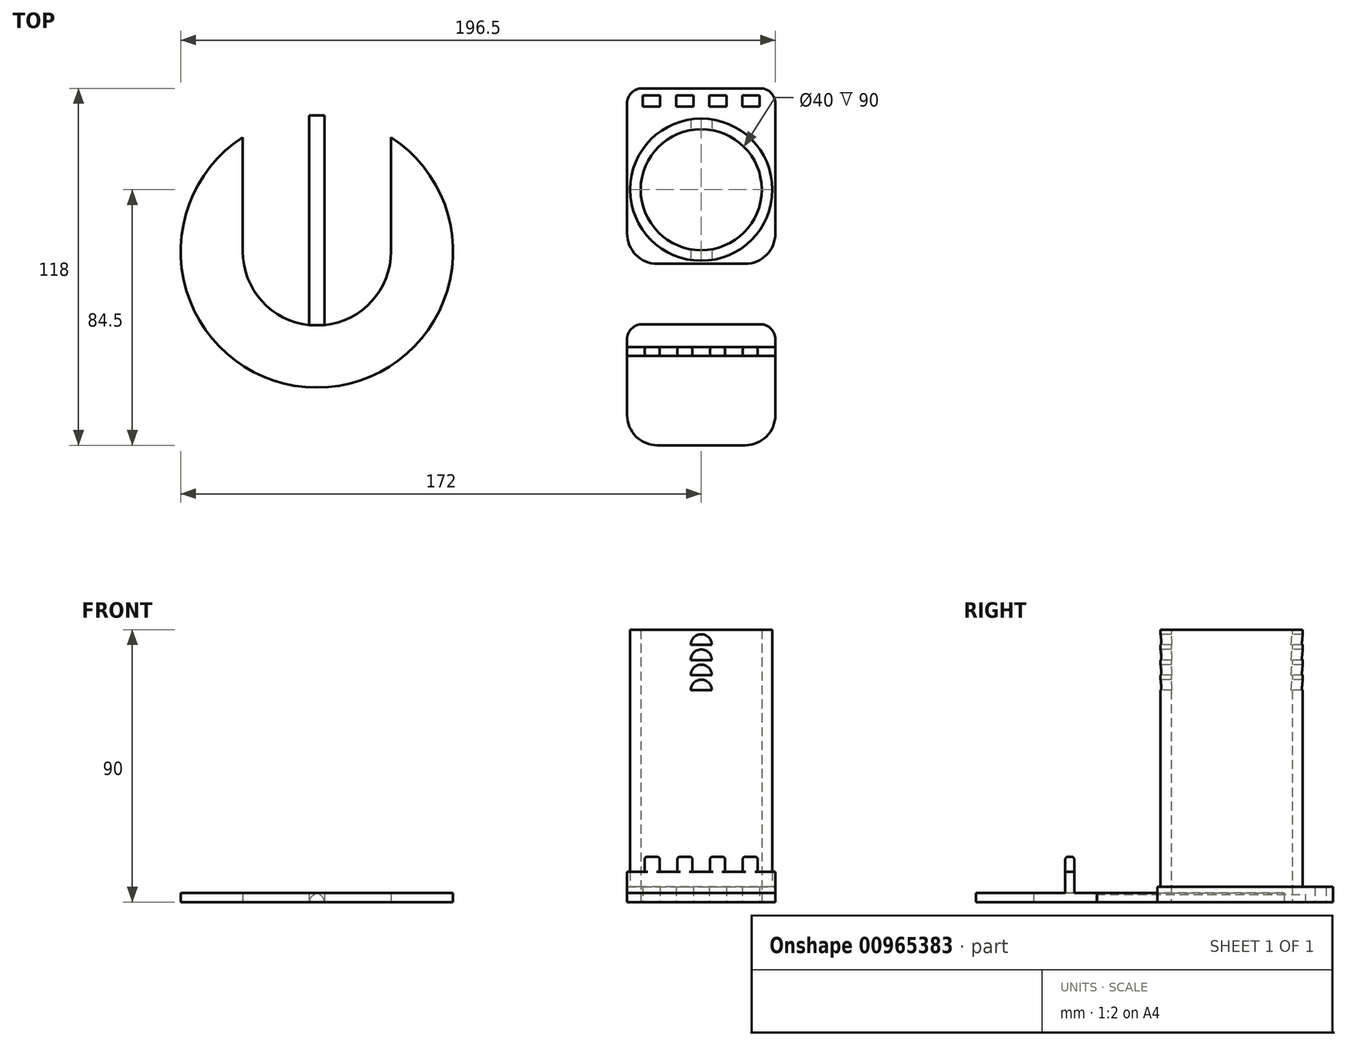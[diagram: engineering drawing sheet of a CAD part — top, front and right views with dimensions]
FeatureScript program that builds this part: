
annotation { "Feature Type Name" : "Feature", "Feature Type Description" : "" }
export const myFeature = defineFeature(function(context is Context, id is Id, definition is map)
    precondition{}
    {
        {
            var Q0;
            Q0=qCreatedBy(makeId("Top.planeOp"),FACE);
            var sketch = newSketch(context, id + "F0", { "sketchPlane" : qUnion([Q0])});
            skLineSegment(sketch, "E0.bottom", {"start": v(0, 0) * mm, "end": v(49, 0) * mm});
            skLineSegment(sketch, "E0.top", {"start": v(0, 40) * mm, "end": v(49, 40) * mm});
            skLineSegment(sketch, "E0.left", {"start": v(0, 0) * mm, "end": v(0, 40) * mm});
            skLineSegment(sketch, "E0.right", {"start": v(49, 0) * mm, "end": v(49, 40) * mm});
            skLineSegment(sketch, "E1.bottom", {"start": v(5.8, 32.5) * mm, "end": v(10.8, 32.5) * mm});
            skLineSegment(sketch, "E1.top", {"start": v(5.8, 29.5) * mm, "end": v(10.8, 29.5) * mm});
            skLineSegment(sketch, "E1.left", {"start": v(5.8, 32.5) * mm, "end": v(5.8, 29.5) * mm});
            skLineSegment(sketch, "E1.right", {"start": v(10.8, 32.5) * mm, "end": v(10.8, 29.5) * mm});
            skLineSegment(sketch, "E2.bottom", {"start": v(16.6, 32.5) * mm, "end": v(21.6, 32.5) * mm});
            skLineSegment(sketch, "E2.top", {"start": v(16.6, 29.5) * mm, "end": v(21.6, 29.5) * mm});
            skLineSegment(sketch, "E2.left", {"start": v(16.6, 32.5) * mm, "end": v(16.6, 29.5) * mm});
            skLineSegment(sketch, "E2.right", {"start": v(21.6, 32.5) * mm, "end": v(21.6, 29.5) * mm});
            skLineSegment(sketch, "E3.bottom", {"start": v(27.4, 32.5) * mm, "end": v(32.4, 32.5) * mm});
            skLineSegment(sketch, "E3.top", {"start": v(27.4, 29.5) * mm, "end": v(32.4, 29.5) * mm});
            skLineSegment(sketch, "E3.left", {"start": v(27.4, 32.5) * mm, "end": v(27.4, 29.5) * mm});
            skLineSegment(sketch, "E3.right", {"start": v(32.4, 32.5) * mm, "end": v(32.4, 29.5) * mm});
            skLineSegment(sketch, "E4.bottom", {"start": v(38.2, 32.5) * mm, "end": v(43.2, 32.5) * mm});
            skLineSegment(sketch, "E4.top", {"start": v(38.2, 29.5) * mm, "end": v(43.2, 29.5) * mm});
            skLineSegment(sketch, "E4.left", {"start": v(38.2, 32.5) * mm, "end": v(38.2, 29.5) * mm});
            skLineSegment(sketch, "E4.right", {"start": v(43.2, 32.5) * mm, "end": v(43.2, 29.5) * mm});
            skLineSegment(sketch, "E5", {"start": v(10.8, 32.5) * mm, "end": v(16.6, 32.5) * mm});
            skLineSegment(sketch, "E6", {"start": v(21.6, 32.5) * mm, "end": v(27.4, 32.5) * mm});
            skLineSegment(sketch, "E7", {"start": v(32.4, 32.5) * mm, "end": v(38.2, 32.5) * mm});
            skLineSegment(sketch, "E8", {"start": v(38.2, 29.5) * mm, "end": v(32.4, 29.5) * mm});
            skLineSegment(sketch, "E9", {"start": v(27.4, 29.5) * mm, "end": v(21.6, 29.5) * mm});
            skLineSegment(sketch, "E10", {"start": v(16.6, 29.5) * mm, "end": v(10.8, 29.5) * mm});
            skLineSegment(sketch, "E11", {"start": v(5.8, 32.5) * mm, "end": v(0, 32.5) * mm});
            skLineSegment(sketch, "E12", {"start": v(5.8, 29.5) * mm, "end": v(0, 29.5) * mm});
            skLineSegment(sketch, "E13", {"start": v(43.2, 32.5) * mm, "end": v(49, 32.5) * mm});
            skLineSegment(sketch, "E14", {"start": v(43.2, 29.5) * mm, "end": v(49, 29.5) * mm});
            skLineSegment(sketch, "E15.bottom", {"start": v(0, 109) * mm, "end": v(49, 109) * mm, "construction": true});
            skLineSegment(sketch, "E15.top", {"start": v(0, 60) * mm, "end": v(49, 60) * mm});
            skLineSegment(sketch, "E15.left", {"start": v(0, 109) * mm, "end": v(0, 60) * mm});
            skLineSegment(sketch, "E15.right", {"start": v(49, 109) * mm, "end": v(49, 60) * mm});
            skLineSegment(sketch, "E16", {"start": v(0, 60) * mm, "end": v(0, 40) * mm, "construction": true});
            skLineSegment(sketch, "E17", {"start": v(0, 109) * mm, "end": v(49, 60) * mm, "construction": true});
            skCircle(sketch, "E18", {"center": v(24.5, 84.5) * mm, "radius": 23.5 * mm});
            skCircle(sketch, "E19", {"center": v(24.5, 84.5) * mm, "radius": 20 * mm});
            skLineSegment(sketch, "E20", {"start": v(0, 109) * mm, "end": v(0, 118) * mm});
            skLineSegment(sketch, "E21", {"start": v(0, 118) * mm, "end": v(49, 118) * mm});
            skLineSegment(sketch, "E22", {"start": v(49, 118) * mm, "end": v(49, 109) * mm});
            skLineSegment(sketch, "E23.bottom", {"start": v(5.24, 115.7) * mm, "end": v(10.94, 115.7) * mm});
            skLineSegment(sketch, "E23.top", {"start": v(5.24, 112) * mm, "end": v(10.94, 112) * mm});
            skLineSegment(sketch, "E23.left", {"start": v(5.24, 115.7) * mm, "end": v(5.24, 112) * mm});
            skLineSegment(sketch, "E23.right", {"start": v(10.94, 115.7) * mm, "end": v(10.94, 112) * mm});
            skLineSegment(sketch, "E24.bottom", {"start": v(16.18, 115.7) * mm, "end": v(21.88, 115.7) * mm});
            skLineSegment(sketch, "E24.top", {"start": v(16.18, 112) * mm, "end": v(21.88, 112) * mm});
            skLineSegment(sketch, "E24.left", {"start": v(16.18, 115.7) * mm, "end": v(16.18, 112) * mm});
            skLineSegment(sketch, "E24.right", {"start": v(21.88, 115.7) * mm, "end": v(21.88, 112) * mm});
            skLineSegment(sketch, "E25.bottom", {"start": v(27.12, 115.7) * mm, "end": v(32.82, 115.7) * mm});
            skLineSegment(sketch, "E25.top", {"start": v(27.12, 112) * mm, "end": v(32.82, 112) * mm});
            skLineSegment(sketch, "E25.left", {"start": v(27.12, 115.7) * mm, "end": v(27.12, 112) * mm});
            skLineSegment(sketch, "E25.right", {"start": v(32.82, 115.7) * mm, "end": v(32.82, 112) * mm});
            skLineSegment(sketch, "E26.bottom", {"start": v(38.06, 115.7) * mm, "end": v(43.76, 115.7) * mm});
            skLineSegment(sketch, "E26.top", {"start": v(38.06, 112) * mm, "end": v(43.76, 112) * mm});
            skLineSegment(sketch, "E26.left", {"start": v(38.06, 115.7) * mm, "end": v(38.06, 112) * mm});
            skLineSegment(sketch, "E26.right", {"start": v(43.76, 115.7) * mm, "end": v(43.76, 112) * mm});
            skLineSegment(sketch, "E27", {"start": v(10.94, 115.7) * mm, "end": v(16.18, 115.7) * mm, "construction": true});
            skLineSegment(sketch, "E28", {"start": v(21.88, 115.7) * mm, "end": v(27.12, 115.7) * mm, "construction": true});
            skLineSegment(sketch, "E29", {"start": v(32.82, 115.7) * mm, "end": v(38.06, 115.7) * mm, "construction": true});
            skLineSegment(sketch, "E30", {"start": v(38.06, 112) * mm, "end": v(32.82, 112) * mm, "construction": true});
            skLineSegment(sketch, "E31", {"start": v(27.12, 112) * mm, "end": v(21.88, 112) * mm, "construction": true});
            skLineSegment(sketch, "E32", {"start": v(16.18, 112) * mm, "end": v(10.94, 112) * mm, "construction": true});
            skLineSegment(sketch, "E33", {"start": v(5.24, 115.7) * mm, "end": v(0, 115.7) * mm, "construction": true});
            skLineSegment(sketch, "E34", {"start": v(5.24, 112) * mm, "end": v(0, 112) * mm, "construction": true});
            skLineSegment(sketch, "E35", {"start": v(43.76, 115.7) * mm, "end": v(49, 115.7) * mm, "construction": true});
            skLineSegment(sketch, "E36", {"start": v(43.76, 112) * mm, "end": v(49, 112) * mm, "construction": true});
            skArc(sketch, "E37", {"start": v(-100, 109) * mm, "mid": v(-102.5, 109.07) * mm, "end": v(-105, 109) * mm, "construction": true});
            skLineSegment(sketch, "E38", {"start": v(-78, 64.07) * mm, "end": v(-78, 101.82) * mm});
            skLineSegment(sketch, "E39", {"start": v(-127, 64.07) * mm, "end": v(-127, 101.82) * mm});
            skLineSegment(sketch, "E40", {"start": v(-100, 39.7) * mm, "end": v(-100, 109) * mm});
            skLineSegment(sketch, "E41", {"start": v(-105, 109) * mm, "end": v(-105, 39.7) * mm});
            skArc(sketch, "E42.trimOffspring", {"start": v(-127, 101.82) * mm, "mid": v(-102.5, 19.07) * mm, "end": v(-78, 101.82) * mm});
            skArc(sketch, "E43.trimOffspring", {"start": v(-127, 64.07) * mm, "mid": v(-120.69, 47.65) * mm, "end": v(-105, 39.7) * mm});
            skArc(sketch, "E44.trimOffspring", {"start": v(-100, 39.7) * mm, "mid": v(-84.31, 47.65) * mm, "end": v(-78, 64.07) * mm});
            skLineSegment(sketch, "E45", {"start": v(-105, 109) * mm, "end": v(-100, 109) * mm});
            skLineSegment(sketch, "E46", {"start": v(0, 109) * mm, "end": v(-100, 109) * mm, "construction": true});
            skSolve(sketch);
        }
        {
            var Q0;
            Q0=makeQuery(id+"F0.imprint","IMPRINT",FACE,{"disambiguationData":[TD([[makeQuery(id+"F0.imprint","IMPRINT",EDGE,{"derivedFrom":sQuery(id+"F0.wireOp",EDGE,"E1.left")}),-1.0]])]});
            var Q1;
            Q1=makeQuery(id+"F0.imprint","IMPRINT",FACE,{"disambiguationData":[TD([[makeQuery(id+"F0.imprint","IMPRINT",EDGE,{"derivedFrom":sQuery(id+"F0.wireOp",EDGE,"E1.bottom")}),-1.0]])]});
            var Q2;
            Q2=makeQuery(id+"F0.imprint","IMPRINT",FACE,{"disambiguationData":[TD([[makeQuery(id+"F0.imprint","IMPRINT",EDGE,{"derivedFrom":sQuery(id+"F0.wireOp",EDGE,"E2.bottom")}),-1.0]])]});
            var Q3;
            Q3=makeQuery(id+"F0.imprint","IMPRINT",FACE,{"disambiguationData":[TD([[makeQuery(id+"F0.imprint","IMPRINT",EDGE,{"derivedFrom":sQuery(id+"F0.wireOp",EDGE,"E3.bottom")}),-1.0]])]});
            var Q4;
            Q4=makeQuery(id+"F0.imprint","IMPRINT",FACE,{"disambiguationData":[TD([[makeQuery(id+"F0.imprint","IMPRINT",EDGE,{"derivedFrom":sQuery(id+"F0.wireOp",EDGE,"E4.bottom")}),-1.0]])]});
            var Q5;
            {var subQ1=sQuery(id+"F0.wireOp",EDGE,"E0.bottom");Q5=makeQuery(id+"F0.imprint","IMPRINT",FACE,{"disambiguationData":[TD([[makeQuery(id+"F0.imprint","IMPRINT",EDGE,{"derivedFrom":subQ1}),1.0]])]});}
            var Q6;
            Q6=makeQuery(id+"F0.imprint","IMPRINT",FACE,{"disambiguationData":[TD([[makeQuery(id+"F0.imprint","IMPRINT",EDGE,{"derivedFrom":sQuery(id+"F0.wireOp",EDGE,"E1.right")}),1.0]])]});
            var Q7;
            Q7=makeQuery(id+"F0.imprint","IMPRINT",FACE,{"disambiguationData":[TD([[makeQuery(id+"F0.imprint","IMPRINT",EDGE,{"derivedFrom":sQuery(id+"F0.wireOp",EDGE,"E2.right")}),1.0]])]});
            var Q8;
            Q8=makeQuery(id+"F0.imprint","IMPRINT",FACE,{"disambiguationData":[TD([[makeQuery(id+"F0.imprint","IMPRINT",EDGE,{"derivedFrom":sQuery(id+"F0.wireOp",EDGE,"E3.right")}),1.0]])]});
            var Q9;
            Q9=makeQuery(id+"F0.imprint","IMPRINT",FACE,{"disambiguationData":[TD([[makeQuery(id+"F0.imprint","IMPRINT",EDGE,{"derivedFrom":sQuery(id+"F0.wireOp",EDGE,"E4.right")}),1.0]])]});
            var Q10;
            {var subQ0=sQuery(id+"F0.wireOp",EDGE,"E0.top");Q10=makeQuery(id+"F0.imprint","IMPRINT",FACE,{"disambiguationData":[TD([[makeQuery(id+"F0.imprint","IMPRINT",EDGE,{"derivedFrom":subQ0}),-1.0]])]});}
            var Q11;
            Q11=makeQuery(id+"F0.imprint","IMPRINT",FACE,{"disambiguationData":[TD([[makeQuery(id+"F0.imprint","IMPRINT",EDGE,{"derivedFrom":sQuery(id+"F0.wireOp",EDGE,"E38")}),-1.0]])]});
            extrude(context, id + "F1", {"entities" : qUnion([Q0, Q1, Q2, Q3, Q4, Q5, Q6, Q7, Q8, Q9, Q10, Q11]), "depth" : 3 * mm, "offsetDistance" : 25 * mm});
        }
        {
            var Q0;
            Q0=makeQuery(id+"F0.imprint","IMPRINT",FACE,{"disambiguationData":[TD([[makeQuery(id+"F0.imprint","IMPRINT",EDGE,{"derivedFrom":sQuery(id+"F0.wireOp",EDGE,"E1.bottom")}),-1.0]])]});
            var Q1;
            Q1=makeQuery(id+"F0.imprint","IMPRINT",FACE,{"disambiguationData":[TD([[makeQuery(id+"F0.imprint","IMPRINT",EDGE,{"derivedFrom":sQuery(id+"F0.wireOp",EDGE,"E2.bottom")}),-1.0]])]});
            var Q2;
            Q2=makeQuery(id+"F0.imprint","IMPRINT",FACE,{"disambiguationData":[TD([[makeQuery(id+"F0.imprint","IMPRINT",EDGE,{"derivedFrom":sQuery(id+"F0.wireOp",EDGE,"E3.bottom")}),-1.0]])]});
            var Q3;
            Q3=makeQuery(id+"F0.imprint","IMPRINT",FACE,{"disambiguationData":[TD([[makeQuery(id+"F0.imprint","IMPRINT",EDGE,{"derivedFrom":sQuery(id+"F0.wireOp",EDGE,"E4.bottom")}),-1.0]])]});
            extrude(context, id + "F2", {"entities" : qUnion([Q0, Q1, Q2, Q3]), "operationType" : NewBodyOperationType.ADD, "depth" : 15 * mm, "offsetDistance" : 25 * mm});
        }
        {
            var Q0;
            Q0=makeQuery(id+"F0.imprint","IMPRINT",FACE,{"disambiguationData":[TD([[makeQuery(id+"F0.imprint","IMPRINT",EDGE,{"derivedFrom":sQuery(id+"F0.wireOp",EDGE,"E1.left")}),-1.0]])]});
            var Q1;
            Q1=makeQuery(id+"F0.imprint","IMPRINT",FACE,{"disambiguationData":[TD([[makeQuery(id+"F0.imprint","IMPRINT",EDGE,{"derivedFrom":sQuery(id+"F0.wireOp",EDGE,"E1.right")}),1.0]])]});
            var Q2;
            Q2=makeQuery(id+"F0.imprint","IMPRINT",FACE,{"disambiguationData":[TD([[makeQuery(id+"F0.imprint","IMPRINT",EDGE,{"derivedFrom":sQuery(id+"F0.wireOp",EDGE,"E2.right")}),1.0]])]});
            var Q3;
            Q3=makeQuery(id+"F0.imprint","IMPRINT",FACE,{"disambiguationData":[TD([[makeQuery(id+"F0.imprint","IMPRINT",EDGE,{"derivedFrom":sQuery(id+"F0.wireOp",EDGE,"E3.right")}),1.0]])]});
            var Q4;
            Q4=makeQuery(id+"F0.imprint","IMPRINT",FACE,{"disambiguationData":[TD([[makeQuery(id+"F0.imprint","IMPRINT",EDGE,{"derivedFrom":sQuery(id+"F0.wireOp",EDGE,"E4.right")}),1.0]])]});
            extrude(context, id + "F3", {"entities" : qUnion([Q0, Q1, Q2, Q3, Q4]), "operationType" : NewBodyOperationType.ADD, "depth" : 10 * mm, "offsetDistance" : 25 * mm});
        }
        {
            var Q0;
            Q0=makeQuery(id+"F0.imprint","IMPRINT",FACE,{"disambiguationData":[TD([[makeQuery(id+"F0.imprint","IMPRINT",EDGE,{"derivedFrom":sQuery(id+"F0.wireOp",EDGE,"E15.top")}),1.0]])]});
            var Q1;
            Q1=makeQuery(id+"F0.imprint","IMPRINT",FACE,{"disambiguationData":[TD([[makeQuery(id+"F0.imprint","IMPRINT",EDGE,{"derivedFrom":sQuery(id+"F0.wireOp",EDGE,"E18")}),1.0]])]});
            extrude(context, id + "F4", {"entities" : qUnion([Q0, Q1]), "depth" : 5 * mm, "offsetDistance" : 25 * mm});
        }
        {
            var Q0;
            Q0=makeQuery(id+"F0.imprint","IMPRINT",FACE,{"disambiguationData":[TD([[makeQuery(id+"F0.imprint","IMPRINT",EDGE,{"derivedFrom":sQuery(id+"F0.wireOp",EDGE,"E18")}),1.0]])]});
            extrude(context, id + "F5", {"entities" : qUnion([Q0]), "operationType" : NewBodyOperationType.ADD, "depth" : 90 * mm, "offsetDistance" : 25 * mm});
        }
        {
            var Q0;
            Q0=qCreatedBy(makeId("Front.planeOp"),FACE);
            var sketch = newSketch(context, id + "F6", { "sketchPlane" : qUnion([Q0])});
            skLineSegment(sketch, "E47", {"start": v(24.5, 90) * mm, "end": v(24.5, 85) * mm, "construction": true});
            skLineSegment(sketch, "E48", {"start": v(24.5, 85) * mm, "end": v(24.5, 80) * mm, "construction": true});
            skLineSegment(sketch, "E49", {"start": v(24.5, 80) * mm, "end": v(24.5, 75) * mm, "construction": true});
            skLineSegment(sketch, "E50", {"start": v(21, 75) * mm, "end": v(28, 75) * mm});
            skArc(sketch, "E51", {"start": v(28, 75) * mm, "mid": v(24.5, 78.5) * mm, "end": v(21, 75) * mm});
            skLineSegment(sketch, "E52", {"start": v(21, 85) * mm, "end": v(28, 85) * mm});
            skArc(sketch, "E53", {"start": v(28, 85) * mm, "mid": v(24.5, 88.5) * mm, "end": v(21, 85) * mm});
            skLineSegment(sketch, "E54", {"start": v(21, 80) * mm, "end": v(28, 80) * mm});
            skArc(sketch, "E55", {"start": v(28, 80) * mm, "mid": v(24.5, 83.5) * mm, "end": v(21, 80) * mm});
            skLineSegment(sketch, "E56", {"start": v(24.5, 75) * mm, "end": v(24.5, 70) * mm, "construction": true});
            skLineSegment(sketch, "E57", {"start": v(21, 70) * mm, "end": v(28, 70) * mm});
            skArc(sketch, "E58", {"start": v(28, 70) * mm, "mid": v(24.5, 73.5) * mm, "end": v(21, 70) * mm});
            skSolve(sketch);
        }
        {
            var Q0;
            Q0=makeQuery(id+"F2.opExtrude","CAP_FACE",FACE,{"disambiguationData":[OSD([sQuery(id+"F0.wireOp",EDGE,"E1.bottom"),sQuery(id+"F0.wireOp",EDGE,"E1.top"),sQuery(id+"F0.wireOp",EDGE,"E1.left"),sQuery(id+"F0.wireOp",EDGE,"E1.right")])],"isStart":false});
            var Q1;
            Q1=makeQuery(id+"F2.opExtrude","CAP_FACE",FACE,{"disambiguationData":[OSD([sQuery(id+"F0.wireOp",EDGE,"E2.bottom"),sQuery(id+"F0.wireOp",EDGE,"E2.top"),sQuery(id+"F0.wireOp",EDGE,"E2.left"),sQuery(id+"F0.wireOp",EDGE,"E2.right")])],"isStart":false});
            var Q2;
            Q2=makeQuery(id+"F2.opExtrude","CAP_FACE",FACE,{"disambiguationData":[OSD([sQuery(id+"F0.wireOp",EDGE,"E3.bottom"),sQuery(id+"F0.wireOp",EDGE,"E3.top"),sQuery(id+"F0.wireOp",EDGE,"E3.left"),sQuery(id+"F0.wireOp",EDGE,"E3.right")])],"isStart":false});
            var Q3;
            Q3=makeQuery(id+"F2.opExtrude","CAP_FACE",FACE,{"disambiguationData":[OSD([sQuery(id+"F0.wireOp",EDGE,"E4.bottom"),sQuery(id+"F0.wireOp",EDGE,"E4.top"),sQuery(id+"F0.wireOp",EDGE,"E4.left"),sQuery(id+"F0.wireOp",EDGE,"E4.right")])],"isStart":false});
            var Q4;
            Q4=makeQuery(id+"F2.opExtrude","SWEPT_EDGE",EDGE,{"disambiguationData":[OSD([sQuery(id+"F0.wireOp",EDGE,"E1.top"),sQuery(id+"F0.wireOp",EDGE,"E1.left")])]});
            var Q5;
            Q5=makeQuery(id+"F2.opExtrude","SWEPT_EDGE",EDGE,{"disambiguationData":[OSD([sQuery(id+"F0.wireOp",EDGE,"E1.top"),sQuery(id+"F0.wireOp",EDGE,"E1.right")])]});
            var Q6;
            Q6=makeQuery(id+"F2.opExtrude","SWEPT_EDGE",EDGE,{"disambiguationData":[OSD([sQuery(id+"F0.wireOp",EDGE,"E2.top"),sQuery(id+"F0.wireOp",EDGE,"E2.left")])]});
            var Q7;
            Q7=makeQuery(id+"F2.opExtrude","SWEPT_EDGE",EDGE,{"disambiguationData":[OSD([sQuery(id+"F0.wireOp",EDGE,"E2.top"),sQuery(id+"F0.wireOp",EDGE,"E2.right")])]});
            var Q8;
            Q8=makeQuery(id+"F2.opExtrude","SWEPT_EDGE",EDGE,{"disambiguationData":[OSD([sQuery(id+"F0.wireOp",EDGE,"E3.top"),sQuery(id+"F0.wireOp",EDGE,"E3.left")])]});
            var Q9;
            Q9=makeQuery(id+"F2.opExtrude","SWEPT_EDGE",EDGE,{"disambiguationData":[OSD([sQuery(id+"F0.wireOp",EDGE,"E3.top"),sQuery(id+"F0.wireOp",EDGE,"E3.right")])]});
            var Q10;
            Q10=makeQuery(id+"F2.opExtrude","SWEPT_EDGE",EDGE,{"disambiguationData":[OSD([sQuery(id+"F0.wireOp",EDGE,"E4.top"),sQuery(id+"F0.wireOp",EDGE,"E4.left")])]});
            var Q11;
            Q11=makeQuery(id+"F2.opExtrude","SWEPT_EDGE",EDGE,{"disambiguationData":[OSD([sQuery(id+"F0.wireOp",EDGE,"E4.top"),sQuery(id+"F0.wireOp",EDGE,"E4.right")])]});
            var Q12;
            Q12=makeQuery(id+"F2.opExtrude","SWEPT_EDGE",EDGE,{"disambiguationData":[OSD([sQuery(id+"F0.wireOp",EDGE,"E4.bottom"),sQuery(id+"F0.wireOp",EDGE,"E4.right")])]});
            var Q13;
            Q13=makeQuery(id+"F2.opExtrude","SWEPT_EDGE",EDGE,{"disambiguationData":[OSD([sQuery(id+"F0.wireOp",EDGE,"E4.bottom"),sQuery(id+"F0.wireOp",EDGE,"E4.left")])]});
            var Q14;
            Q14=makeQuery(id+"F2.opExtrude","SWEPT_EDGE",EDGE,{"disambiguationData":[OSD([sQuery(id+"F0.wireOp",EDGE,"E3.bottom"),sQuery(id+"F0.wireOp",EDGE,"E3.right")])]});
            var Q15;
            Q15=makeQuery(id+"F2.opExtrude","SWEPT_EDGE",EDGE,{"disambiguationData":[OSD([sQuery(id+"F0.wireOp",EDGE,"E3.bottom"),sQuery(id+"F0.wireOp",EDGE,"E3.left")])]});
            var Q16;
            Q16=makeQuery(id+"F2.opExtrude","SWEPT_EDGE",EDGE,{"disambiguationData":[OSD([sQuery(id+"F0.wireOp",EDGE,"E2.bottom"),sQuery(id+"F0.wireOp",EDGE,"E2.right")])]});
            var Q17;
            Q17=makeQuery(id+"F2.opExtrude","SWEPT_EDGE",EDGE,{"disambiguationData":[OSD([sQuery(id+"F0.wireOp",EDGE,"E2.bottom"),sQuery(id+"F0.wireOp",EDGE,"E2.left")])]});
            var Q18;
            Q18=makeQuery(id+"F2.opExtrude","SWEPT_EDGE",EDGE,{"disambiguationData":[OSD([sQuery(id+"F0.wireOp",EDGE,"E1.bottom"),sQuery(id+"F0.wireOp",EDGE,"E1.right")])]});
            var Q19;
            Q19=makeQuery(id+"F2.opExtrude","SWEPT_EDGE",EDGE,{"disambiguationData":[OSD([sQuery(id+"F0.wireOp",EDGE,"E1.bottom"),sQuery(id+"F0.wireOp",EDGE,"E1.left")])]});
            fillet(context, id + "F7", {"entities" : qUnion([Q0, Q1, Q2, Q3, Q4, Q5, Q6, Q7, Q8, Q9, Q10, Q11, Q12, Q13, Q14, Q15, Q16, Q17, Q18, Q19]), "radius" : 1 * mm, "tangentPropagation" : true, "allowEdgeOverflow" : false});
        }
        {
            var Q0;
            Q0=makeQuery(id+"F1.opExtrude","SWEPT_EDGE",EDGE,{"disambiguationData":[OSD([sQuery(id+"F0.wireOp",EDGE,"E0.top"),sQuery(id+"F0.wireOp",EDGE,"E0.right")])]});
            var Q1;
            Q1=makeQuery(id+"F1.opExtrude","SWEPT_EDGE",EDGE,{"disambiguationData":[OSD([sQuery(id+"F0.wireOp",EDGE,"E0.top"),sQuery(id+"F0.wireOp",EDGE,"E0.left")])]});
            var Q2;
            Q2=makeQuery(id+"F4.opExtrude","SWEPT_EDGE",EDGE,{"disambiguationData":[OSD([sQuery(id+"F0.wireOp",EDGE,"E20"),sQuery(id+"F0.wireOp",EDGE,"E21")])]});
            var Q3;
            Q3=makeQuery(id+"F4.opExtrude","SWEPT_EDGE",EDGE,{"disambiguationData":[OSD([sQuery(id+"F0.wireOp",EDGE,"E21"),sQuery(id+"F0.wireOp",EDGE,"E22")])]});
            fillet(context, id + "F8", {"entities" : qUnion([Q0, Q1, Q2, Q3]), "radius" : 5 * mm, "tangentPropagation" : true, "allowEdgeOverflow" : false});
        }
        {
            var Q0;
            Q0=makeQuery(id+"F1.opExtrude","SWEPT_EDGE",EDGE,{"disambiguationData":[OSD([sQuery(id+"F0.wireOp",EDGE,"E0.bottom"),sQuery(id+"F0.wireOp",EDGE,"E0.left")])]});
            var Q1;
            Q1=makeQuery(id+"F1.opExtrude","SWEPT_EDGE",EDGE,{"disambiguationData":[OSD([sQuery(id+"F0.wireOp",EDGE,"E0.bottom"),sQuery(id+"F0.wireOp",EDGE,"E0.right")])]});
            var Q2;
            Q2=makeQuery(id+"F4.opExtrude","SWEPT_EDGE",EDGE,{"disambiguationData":[OSD([sQuery(id+"F0.wireOp",EDGE,"E15.top"),sQuery(id+"F0.wireOp",EDGE,"E15.left")])]});
            var Q3;
            Q3=makeQuery(id+"F4.opExtrude","SWEPT_EDGE",EDGE,{"disambiguationData":[OSD([sQuery(id+"F0.wireOp",EDGE,"E15.top"),sQuery(id+"F0.wireOp",EDGE,"E15.right")])]});
            fillet(context, id + "F9", {"entities" : qUnion([Q0, Q1, Q2, Q3]), "radius" : 10 * mm, "tangentPropagation" : true, "allowEdgeOverflow" : false});
        }
        {
            var Q0;
            Q0=makeQuery(id+"F1.opExtrude","SWEPT_FACE",FACE,{"disambiguationData":[OSD([sQuery(id+"F0.wireOp",EDGE,"E45")])]});
            var sketch = newSketch(context, id + "F10", { "sketchPlane" : qUnion([Q0])});
            skLineSegment(sketch, "E59", {"start": v(100, 0) * mm, "end": v(105, 0) * mm, "construction": true});
            skArc(sketch, "E60", {"start": v(105, 0) * mm, "mid": v(102.5, 2.5) * mm, "end": v(100, 0) * mm});
            skLineSegment(sketch, "E61", {"start": v(100, 0) * mm, "end": v(100, 3) * mm});
            skLineSegment(sketch, "E62", {"start": v(100, 3) * mm, "end": v(105, 3) * mm});
            skLineSegment(sketch, "E63", {"start": v(105, 3) * mm, "end": v(105, 0) * mm});
            skSolve(sketch);
        }
        {
            var Q0;
            Q0=makeQuery(id+"F10.imprint","IMPRINT",FACE,{"disambiguationData":[TD([[makeQuery(id+"F10.imprint","IMPRINT",EDGE,{"derivedFrom":sQuery(id+"F10.wireOp",EDGE,"E60")}),-1.0]])]});
            var Q1;
            Q1=sQuery(id+"F0.wireOp",VERTEX,"E40.start");
            extrude(context, id + "F11", {"entities" : qUnion([Q0]), "operationType" : NewBodyOperationType.REMOVE, "endBound" : BoundingType.UP_TO_VERTEX, "oppositeDirection" : true, "depth" : 25 * mm, "endBoundEntityVertex" : qUnion([Q1]), "offsetDistance" : 25 * mm});
        }
        {
            var Q0;
            Q0=makeQuery(id+"F6.imprint","IMPRINT",FACE,{"disambiguationData":[TD([[makeQuery(id+"F6.imprint","IMPRINT",EDGE,{"derivedFrom":sQuery(id+"F6.wireOp",EDGE,"E52")}),1.0]])]});
            var Q1;
            Q1=makeQuery(id+"F6.imprint","IMPRINT",FACE,{"disambiguationData":[TD([[makeQuery(id+"F6.imprint","IMPRINT",EDGE,{"derivedFrom":sQuery(id+"F6.wireOp",EDGE,"E54")}),1.0]])]});
            var Q2;
            Q2=makeQuery(id+"F6.imprint","IMPRINT",FACE,{"disambiguationData":[TD([[makeQuery(id+"F6.imprint","IMPRINT",EDGE,{"derivedFrom":sQuery(id+"F6.wireOp",EDGE,"E50")}),1.0]])]});
            var Q3;
            Q3=makeQuery(id+"F6.imprint","IMPRINT",FACE,{"disambiguationData":[TD([[makeQuery(id+"F6.imprint","IMPRINT",EDGE,{"derivedFrom":sQuery(id+"F6.wireOp",EDGE,"E57")}),1.0]])]});
            extrude(context, id + "F12", {"entities" : qUnion([Q0, Q1, Q2, Q3]), "operationType" : NewBodyOperationType.REMOVE, "endBound" : BoundingType.THROUGH_ALL, "oppositeDirection" : true, "depth" : 25 * mm, "offsetDistance" : 25 * mm});
        }
    });
